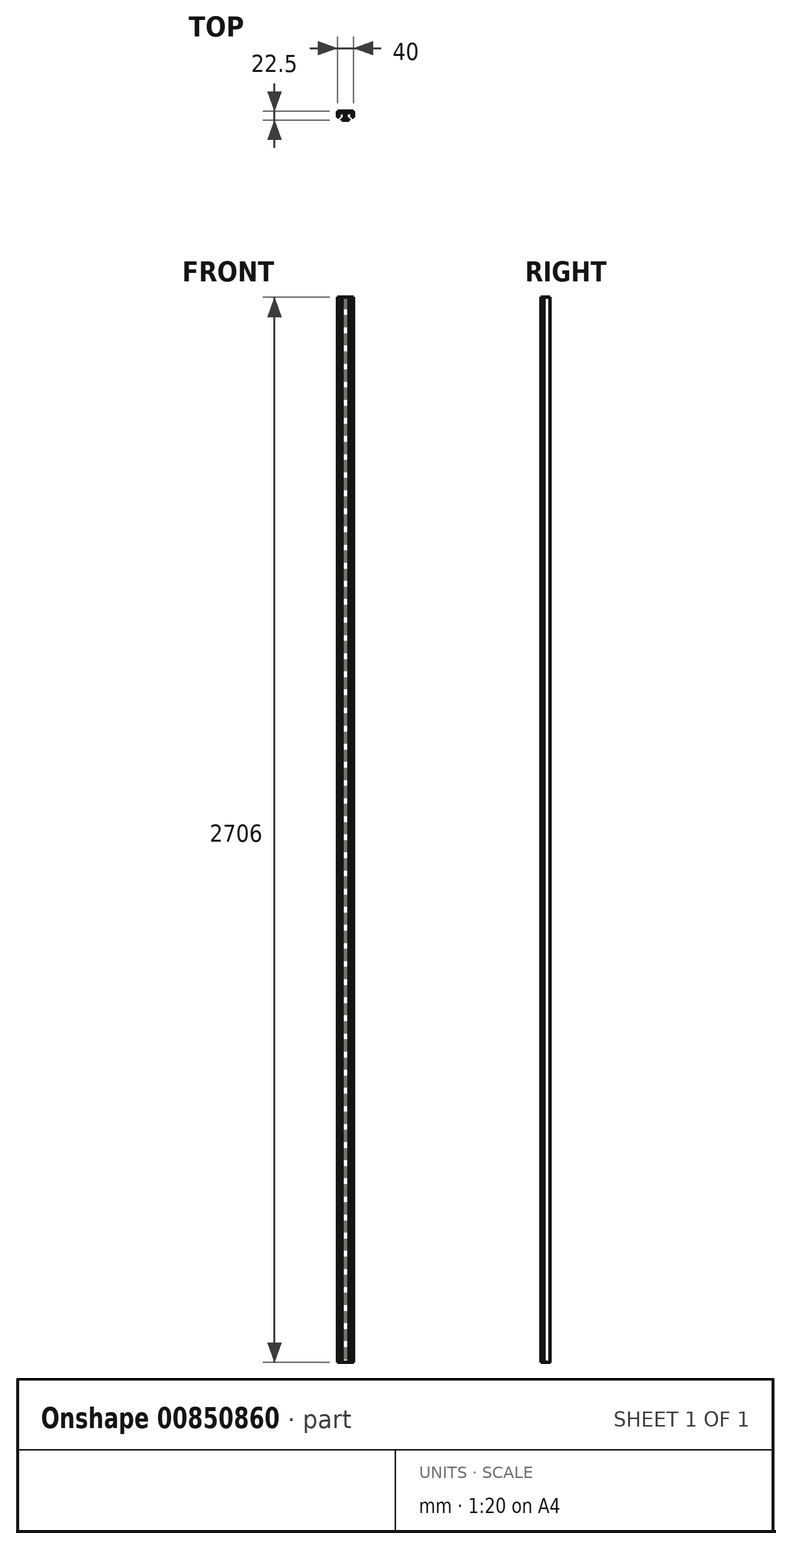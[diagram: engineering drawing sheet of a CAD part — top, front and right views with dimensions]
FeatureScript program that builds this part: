
annotation { "Feature Type Name" : "Feature", "Feature Type Description" : "" }
export const myFeature = defineFeature(function(context is Context, id is Id, definition is map)
    precondition{}
    {
        {
            var Q0;
            Q0=qCreatedBy(makeId("Top.planeOp"),FACE);
            var sketch = newSketch(context, id + "F0", { "sketchPlane" : qUnion([Q0])});
            skLineSegment(sketch, "E0", {"start": v(-20, 10) * mm, "end": v(20, 10) * mm});
            skLineSegment(sketch, "E1", {"start": v(20, 10) * mm, "end": v(20, -5) * mm});
            skLineSegment(sketch, "E2", {"start": v(-20, 10) * mm, "end": v(-20, -5) * mm});
            skLineSegment(sketch, "E3.0", {"start": v(-17, 7) * mm, "end": v(-17, -5) * mm});
            skLineSegment(sketch, "E3.1", {"start": v(-17, 7) * mm, "end": v(-2, 7) * mm});
            skLineSegment(sketch, "E3.2", {"start": v(17, 7) * mm, "end": v(17, -5) * mm});
            skLineSegment(sketch, "E4", {"start": v(-20, -5) * mm, "end": v(-17, -5) * mm});
            skLineSegment(sketch, "E5", {"start": v(17, -5) * mm, "end": v(20, -5) * mm});
            skLineSegment(sketch, "E6", {"start": v(-2, 7) * mm, "end": v(-2, -9.5) * mm});
            skLineSegment(sketch, "E7", {"start": v(-2, -9.5) * mm, "end": v(-8.5, -9.5) * mm});
            skLineSegment(sketch, "E8", {"start": v(-8.5, -9.5) * mm, "end": v(-8.5, -12.5) * mm});
            skLineSegment(sketch, "E9", {"start": v(-8.5, -12.5) * mm, "end": v(0, -12.5) * mm});
            skLineSegment(sketch, "E10.MirrorCS", {"start": v(2, -9.5) * mm, "end": v(8.5, -9.5) * mm});
            skLineSegment(sketch, "E11.MirrorCS", {"start": v(8.5, -12.5) * mm, "end": v(0, -12.5) * mm});
            skLineSegment(sketch, "E12.MirrorCS", {"start": v(8.5, -9.5) * mm, "end": v(8.5, -12.5) * mm});
            skLineSegment(sketch, "E13.MirrorCS", {"start": v(2, 7) * mm, "end": v(2, -9.5) * mm});
            skLineSegment(sketch, "E14.trimOffspring", {"start": v(2, 7) * mm, "end": v(17, 7) * mm});
            skSolve(sketch);
        }
        {
            var Q0;
            Q0=qSketchRegion(id+"F0",true);
            extrude(context, id + "F1", {"entities" : qUnion([Q0]), "depth" : 2706 * mm, "offsetDistance" : 25 * mm});
        }
        {
            var Q0;
            Q0=makeQuery(id+"F1.opExtrude","SWEPT_EDGE",EDGE,{"disambiguationData":[OSD([sQuery(id+"F0.wireOp",EDGE,"E0"),sQuery(id+"F0.wireOp",EDGE,"E2")])]});
            var Q1;
            Q1=makeQuery(id+"F1.opExtrude","SWEPT_EDGE",EDGE,{"disambiguationData":[OSD([sQuery(id+"F0.wireOp",EDGE,"E0"),sQuery(id+"F0.wireOp",EDGE,"E1")])]});
            fillet(context, id + "F2", {"entities" : qUnion([Q0, Q1]), "radius" : 2 * mm, "tangentPropagation" : true, "allowEdgeOverflow" : false});
        }
        {
            var Q0;
            Q0=makeQuery(id+"F1.opExtrude","SWEPT_EDGE",EDGE,{"disambiguationData":[OSD([sQuery(id+"F0.wireOp",EDGE,"E3.0"),sQuery(id+"F0.wireOp",EDGE,"E4")])]});
            var Q1;
            Q1=makeQuery(id+"F1.opExtrude","SWEPT_EDGE",EDGE,{"disambiguationData":[OSD([sQuery(id+"F0.wireOp",EDGE,"E2"),sQuery(id+"F0.wireOp",EDGE,"E4")])]});
            var Q2;
            Q2=makeQuery(id+"F1.opExtrude","SWEPT_EDGE",EDGE,{"disambiguationData":[OSD([sQuery(id+"F0.wireOp",EDGE,"E3.0"),sQuery(id+"F0.wireOp",EDGE,"E3.1")])]});
            var Q3;
            Q3=makeQuery(id+"F1.opExtrude","SWEPT_EDGE",EDGE,{"disambiguationData":[OSD([sQuery(id+"F0.wireOp",EDGE,"E13.MirrorCS"),sQuery(id+"F0.wireOp",EDGE,"E14.trimOffspring")])]});
            var Q4;
            Q4=makeQuery(id+"F1.opExtrude","SWEPT_EDGE",EDGE,{"disambiguationData":[OSD([sQuery(id+"F0.wireOp",EDGE,"E3.2"),sQuery(id+"F0.wireOp",EDGE,"E5")])]});
            var Q5;
            Q5=makeQuery(id+"F1.opExtrude","SWEPT_EDGE",EDGE,{"disambiguationData":[OSD([sQuery(id+"F0.wireOp",EDGE,"E1"),sQuery(id+"F0.wireOp",EDGE,"E5")])]});
            var Q6;
            Q6=makeQuery(id+"F1.opExtrude","SWEPT_EDGE",EDGE,{"disambiguationData":[OSD([sQuery(id+"F0.wireOp",EDGE,"E10.MirrorCS"),sQuery(id+"F0.wireOp",EDGE,"E12.MirrorCS")])]});
            var Q7;
            Q7=makeQuery(id+"F1.opExtrude","SWEPT_EDGE",EDGE,{"disambiguationData":[OSD([sQuery(id+"F0.wireOp",EDGE,"E11.MirrorCS"),sQuery(id+"F0.wireOp",EDGE,"E12.MirrorCS")])]});
            var Q8;
            Q8=makeQuery(id+"F1.opExtrude","SWEPT_EDGE",EDGE,{"disambiguationData":[OSD([sQuery(id+"F0.wireOp",EDGE,"E8"),sQuery(id+"F0.wireOp",EDGE,"E9")])]});
            var Q9;
            Q9=makeQuery(id+"F1.opExtrude","SWEPT_EDGE",EDGE,{"disambiguationData":[OSD([sQuery(id+"F0.wireOp",EDGE,"E7"),sQuery(id+"F0.wireOp",EDGE,"E8")])]});
            var Q10;
            Q10=makeQuery(id+"F1.opExtrude","SWEPT_EDGE",EDGE,{"disambiguationData":[OSD([sQuery(id+"F0.wireOp",EDGE,"E6"),sQuery(id+"F0.wireOp",EDGE,"E7")])]});
            var Q11;
            Q11=makeQuery(id+"F1.opExtrude","SWEPT_EDGE",EDGE,{"disambiguationData":[OSD([sQuery(id+"F0.wireOp",EDGE,"E3.1"),sQuery(id+"F0.wireOp",EDGE,"E6")])]});
            var Q12;
            Q12=makeQuery(id+"F1.opExtrude","SWEPT_EDGE",EDGE,{"disambiguationData":[OSD([sQuery(id+"F0.wireOp",EDGE,"E3.2"),sQuery(id+"F0.wireOp",EDGE,"E14.trimOffspring")])]});
            var Q13;
            Q13=makeQuery(id+"F1.opExtrude","SWEPT_EDGE",EDGE,{"disambiguationData":[OSD([sQuery(id+"F0.wireOp",EDGE,"E10.MirrorCS"),sQuery(id+"F0.wireOp",EDGE,"E13.MirrorCS")])]});
            fillet(context, id + "F3", {"entities" : qUnion([Q0, Q1, Q2, Q3, Q4, Q5, Q6, Q7, Q8, Q9, Q10, Q11, Q12, Q13]), "radius" : 1 * mm, "tangentPropagation" : true, "allowEdgeOverflow" : false});
        }
    });
